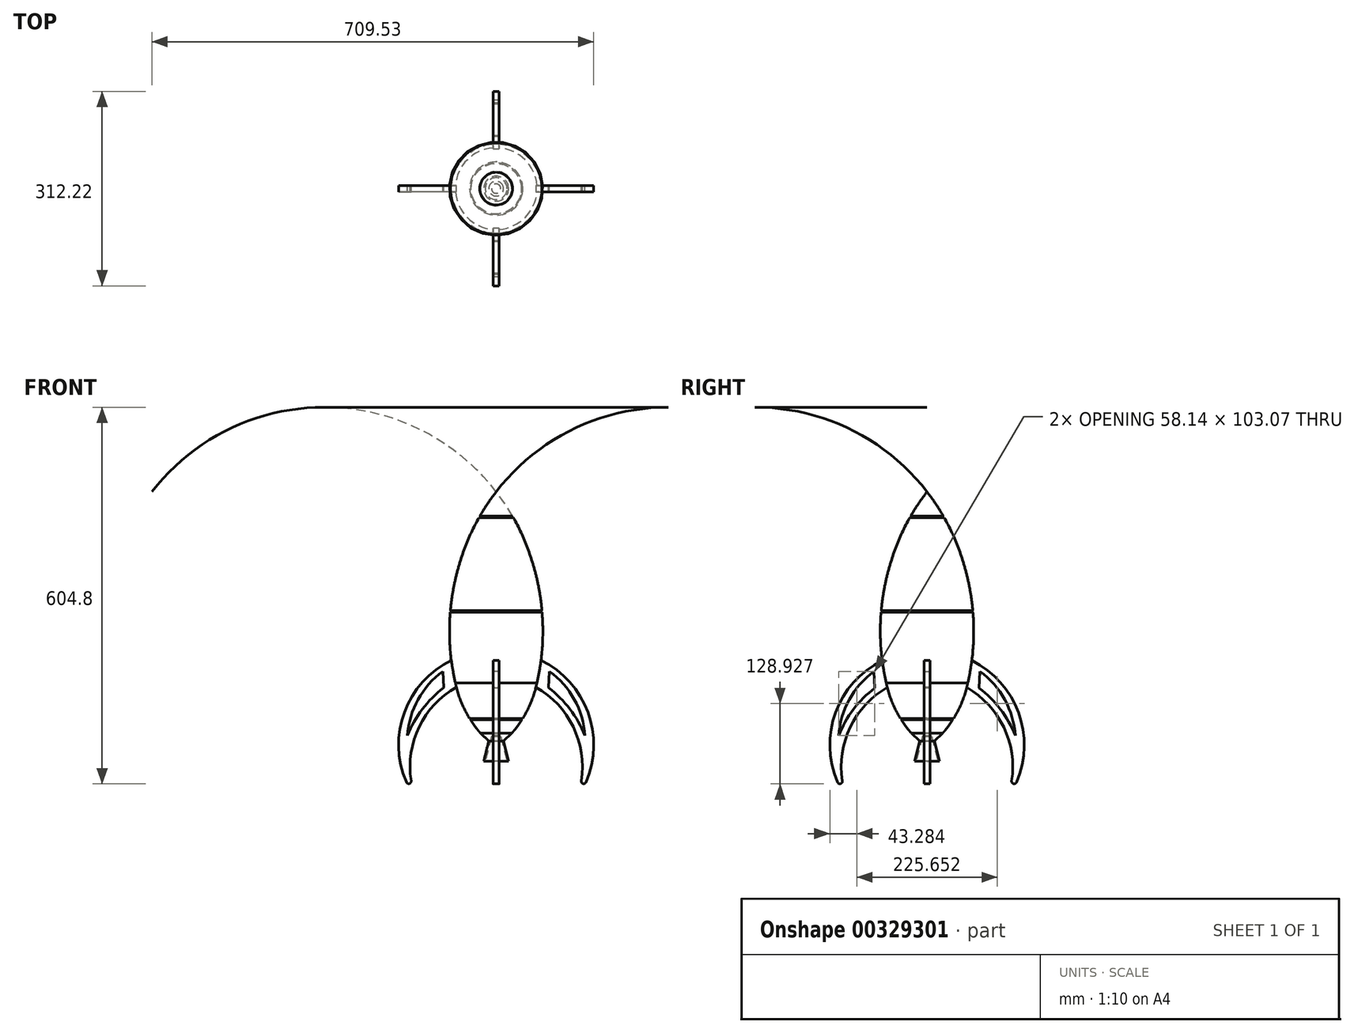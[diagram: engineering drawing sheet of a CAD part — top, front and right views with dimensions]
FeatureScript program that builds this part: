
annotation { "Feature Type Name" : "Feature", "Feature Type Description" : "" }
export const myFeature = defineFeature(function(context is Context, id is Id, definition is map)
    precondition{}
    {
        {
            var Q0;
            Q0=qCreatedBy(makeId("Front.planeOp"),FACE);
            var sketch = newSketch(context, id + "F0", { "sketchPlane" : qUnion([Q0])});
            skLineSegment(sketch, "E0", {"start": v(0, 40) * mm, "end": v(0, 433.08) * mm});
            skLineSegment(sketch, "E1", {"start": v(-20, 0) * mm, "end": v(-17.5, 0) * mm});
            skArc(sketch, "E2", {"start": v(0, 433.08) * mm, "mid": v(-13.77, 413.96) * mm, "end": v(-26.22, 393.96) * mm});
            skArc(sketch, "E3", {"start": v(-58.06, 320.33) * mm, "mid": v(-63.49, 301.11) * mm, "end": v(-67.89, 281.63) * mm});
            skArc(sketch, "E4", {"start": v(-65.64, 125.91) * mm, "mid": v(-56.62, 96.54) * mm, "end": v(-42.76, 69.12) * mm});
            skLineSegment(sketch, "E5", {"start": v(0, 40) * mm, "end": v(-7.5, 40) * mm});
            skLineSegment(sketch, "E6", {"start": v(-17.5, 0) * mm, "end": v(-7.5, 40) * mm});
            skLineSegment(sketch, "E7", {"start": v(-20, 0) * mm, "end": v(-11.84, 32.88) * mm});
            skLineSegment(sketch, "E8", {"start": v(-25.15, 45.22) * mm, "end": v(-11.84, 32.88) * mm});
            skArc(sketch, "E9", {"start": v(-27.56, 391.62) * mm, "mid": v(-25.72, 392.12) * mm, "end": v(-26.22, 393.96) * mm});
            skArc(sketch, "E10.trimOffspring", {"start": v(-29.48, 50.38) * mm, "mid": v(-27.34, 47.78) * mm, "end": v(-25.15, 45.22) * mm});
            skArc(sketch, "E11.trimOffspring", {"start": v(-68.4, 278.98) * mm, "mid": v(-71.4, 260.75) * mm, "end": v(-73.51, 242.4) * mm});
            skArc(sketch, "E12.trimOffspring", {"start": v(-27.56, 391.62) * mm, "mid": v(-44.8, 356.82) * mm, "end": v(-58.06, 320.33) * mm});
            skArc(sketch, "E13", {"start": v(-73.74, 239.7) * mm, "mid": v(-72.28, 240.93) * mm, "end": v(-73.51, 242.4) * mm});
            skLineSegment(sketch, "E14", {"start": v(-68.4, 278.98) * mm, "end": v(-67.89, 281.63) * mm});
            skArc(sketch, "E15.trimOffspring", {"start": v(-73.74, 239.7) * mm, "mid": v(-74.06, 182.5) * mm, "end": v(-65.64, 125.91) * mm});
            skArc(sketch, "E16", {"start": v(-41.32, 66.83) * mm, "mid": v(-40.9, 68.7) * mm, "end": v(-42.76, 69.12) * mm});
            skLineSegment(sketch, "E17", {"start": v(-31.16, 52.5) * mm, "end": v(-29.48, 50.38) * mm});
            skArc(sketch, "E18.trimOffspring", {"start": v(-41.32, 66.83) * mm, "mid": v(-36.41, 59.54) * mm, "end": v(-31.16, 52.5) * mm});
            skSolve(sketch);
        }
        {
            var Q0;
            Q0=makeQuery(id+"F0.imprint","IMPRINT",FACE,{"disambiguationData":[TD([[makeQuery(id+"F0.imprint","IMPRINT",EDGE,{"derivedFrom":sQuery(id+"F0.wireOp",EDGE,"E0")}),1.0]])]});
            var Q1;
            Q1=sQuery(id+"F0.wireOp",EDGE,"E0");
            revolve(context, id + "F1", {"entities" : qUnion([Q0]), "axis" : qUnion([Q1]), "revolveType" : RevolveType.FULL});
        }
        {
            var Q0;
            Q0=qCreatedBy(makeId("Front.planeOp"),FACE);
            var sketch = newSketch(context, id + "F2", { "sketchPlane" : qUnion([Q0])});
            skArc(sketch, "E19", {"start": v(-61.07, 120.74) * mm, "mid": v(-123.07, 56.81) * mm, "end": v(-136.57, -31.21) * mm});
            skArc(sketch, "E20", {"start": v(-65.4, 165.41) * mm, "mid": v(-146.05, 82.34) * mm, "end": v(-144.19, -33.43) * mm});
            skPoint(sketch, "E21.visualSharp", {"position": v(-128.54, -61.08) * mm});
            skArc(sketch, "E21.filletArc", {"start": v(-144.19, -33.43) * mm, "mid": v(-139.4, -35.68) * mm, "end": v(-136.57, -31.21) * mm});
            skArc(sketch, "E22.MirrorCS", {"start": v(61.07, 120.74) * mm, "mid": v(123.07, 56.81) * mm, "end": v(136.57, -31.21) * mm});
            skArc(sketch, "E23.MirrorCS", {"start": v(65.4, 165.41) * mm, "mid": v(146.05, 82.34) * mm, "end": v(144.19, -33.43) * mm});
            skArc(sketch, "E24.MirrorCS", {"start": v(144.19, -33.43) * mm, "mid": v(139.4, -35.68) * mm, "end": v(136.57, -31.21) * mm});
            skLineSegment(sketch, "E25", {"start": v(-61.07, 120.74) * mm, "end": v(-65.4, 165.41) * mm});
            skLineSegment(sketch, "E26", {"start": v(61.07, 120.74) * mm, "end": v(65.4, 165.41) * mm});
            skArc(sketch, "E27", {"start": v(-84.33, 118.2) * mm, "mid": v(-118.66, 83.87) * mm, "end": v(-142.47, 41.56) * mm});
            skArc(sketch, "E28", {"start": v(-85.65, 144.62) * mm, "mid": v(-125.49, 99.4) * mm, "end": v(-142.47, 41.56) * mm});
            skLineSegment(sketch, "E29", {"start": v(-84.33, 118.2) * mm, "end": v(-85.65, 144.62) * mm});
            skArc(sketch, "E30.MirrorCS", {"start": v(84.33, 118.2) * mm, "mid": v(118.66, 83.87) * mm, "end": v(142.47, 41.56) * mm});
            skLineSegment(sketch, "E31.MirrorCS", {"start": v(84.33, 118.2) * mm, "end": v(85.65, 144.62) * mm});
            skArc(sketch, "E32.MirrorCS", {"start": v(85.65, 144.62) * mm, "mid": v(125.49, 99.4) * mm, "end": v(142.47, 41.56) * mm});
            skLineSegment(sketch, "E33", {"start": v(-65.4, 165.41) * mm, "end": v(-65.4, 0) * mm});
            skLineSegment(sketch, "E34", {"start": v(-65.4, 0) * mm, "end": v(0, 0) * mm});
            skSolve(sketch);
        }
        {
            var Q0;
            Q0 = qSketchRegion(id + "F2", true);
            extrude(context, id + "F3", {"entities" : qUnion([Q0]), "operationType" : NewBodyOperationType.ADD, "depth" : 5 * mm, "hasSecondDirection" : true, "secondDirectionOppositeDirection" : true, "secondDirectionDepth" : 5 * mm});
        }
        {
            var Q0;
            Q0=qCreatedBy(makeId("Right.planeOp"),FACE);
            var sketch = newSketch(context, id + "F4", { "sketchPlane" : qUnion([Q0])});
            skArc(sketch, "E35", {"start": v(-60.5, 120.57) * mm, "mid": v(-122.5, 56.64) * mm, "end": v(-136, -31.39) * mm});
            skArc(sketch, "E36", {"start": v(-64.82, 165.24) * mm, "mid": v(-145.48, 82.17) * mm, "end": v(-143.62, -33.6) * mm});
            skPoint(sketch, "E37.visualSharp", {"position": v(-119.97, -130.26) * mm});
            skArc(sketch, "E37.filletArc", {"start": v(-143.62, -33.6) * mm, "mid": v(-138.83, -35.85) * mm, "end": v(-136, -31.39) * mm});
            skLineSegment(sketch, "E38", {"start": v(-60.5, 120.57) * mm, "end": v(-64.82, 165.24) * mm});
            skArc(sketch, "E39", {"start": v(-83.76, 118.02) * mm, "mid": v(-118.09, 83.7) * mm, "end": v(-141.9, 41.38) * mm});
            skArc(sketch, "E40", {"start": v(-85.08, 144.45) * mm, "mid": v(-124.92, 99.22) * mm, "end": v(-141.9, 41.38) * mm});
            skLineSegment(sketch, "E41", {"start": v(-83.76, 118.02) * mm, "end": v(-85.08, 144.45) * mm});
            skLineSegment(sketch, "E42", {"start": v(0, 0) * mm, "end": v(-65.4, 0) * mm});
            skLineSegment(sketch, "E43", {"start": v(-65.4, 0) * mm, "end": v(-65.4, 165.41) * mm});
            skArc(sketch, "E44.MirrorCS", {"start": v(60.5, 120.57) * mm, "mid": v(122.5, 56.64) * mm, "end": v(136, -31.39) * mm});
            skArc(sketch, "E45.MirrorCS", {"start": v(83.76, 118.02) * mm, "mid": v(118.09, 83.7) * mm, "end": v(141.9, 41.38) * mm});
            skArc(sketch, "E46.MirrorCS", {"start": v(85.08, 144.45) * mm, "mid": v(124.92, 99.22) * mm, "end": v(141.9, 41.38) * mm});
            skArc(sketch, "E47.MirrorCS", {"start": v(64.82, 165.24) * mm, "mid": v(145.48, 82.17) * mm, "end": v(143.62, -33.6) * mm});
            skLineSegment(sketch, "E48.MirrorCS", {"start": v(60.5, 120.57) * mm, "end": v(64.82, 165.24) * mm});
            skArc(sketch, "E49.MirrorCS", {"start": v(143.62, -33.6) * mm, "mid": v(138.83, -35.85) * mm, "end": v(136, -31.39) * mm});
            skLineSegment(sketch, "E50.MirrorCS", {"start": v(83.76, 118.02) * mm, "end": v(85.08, 144.45) * mm});
            skSolve(sketch);
        }
        {
            var Q0;
            Q0 = qSketchRegion(id + "F4", true);
            extrude(context, id + "F5", {"entities" : qUnion([Q0]), "operationType" : NewBodyOperationType.ADD, "depth" : 5 * mm, "hasSecondDirection" : true, "secondDirectionOppositeDirection" : true, "secondDirectionDepth" : 5 * mm});
        }
    });
